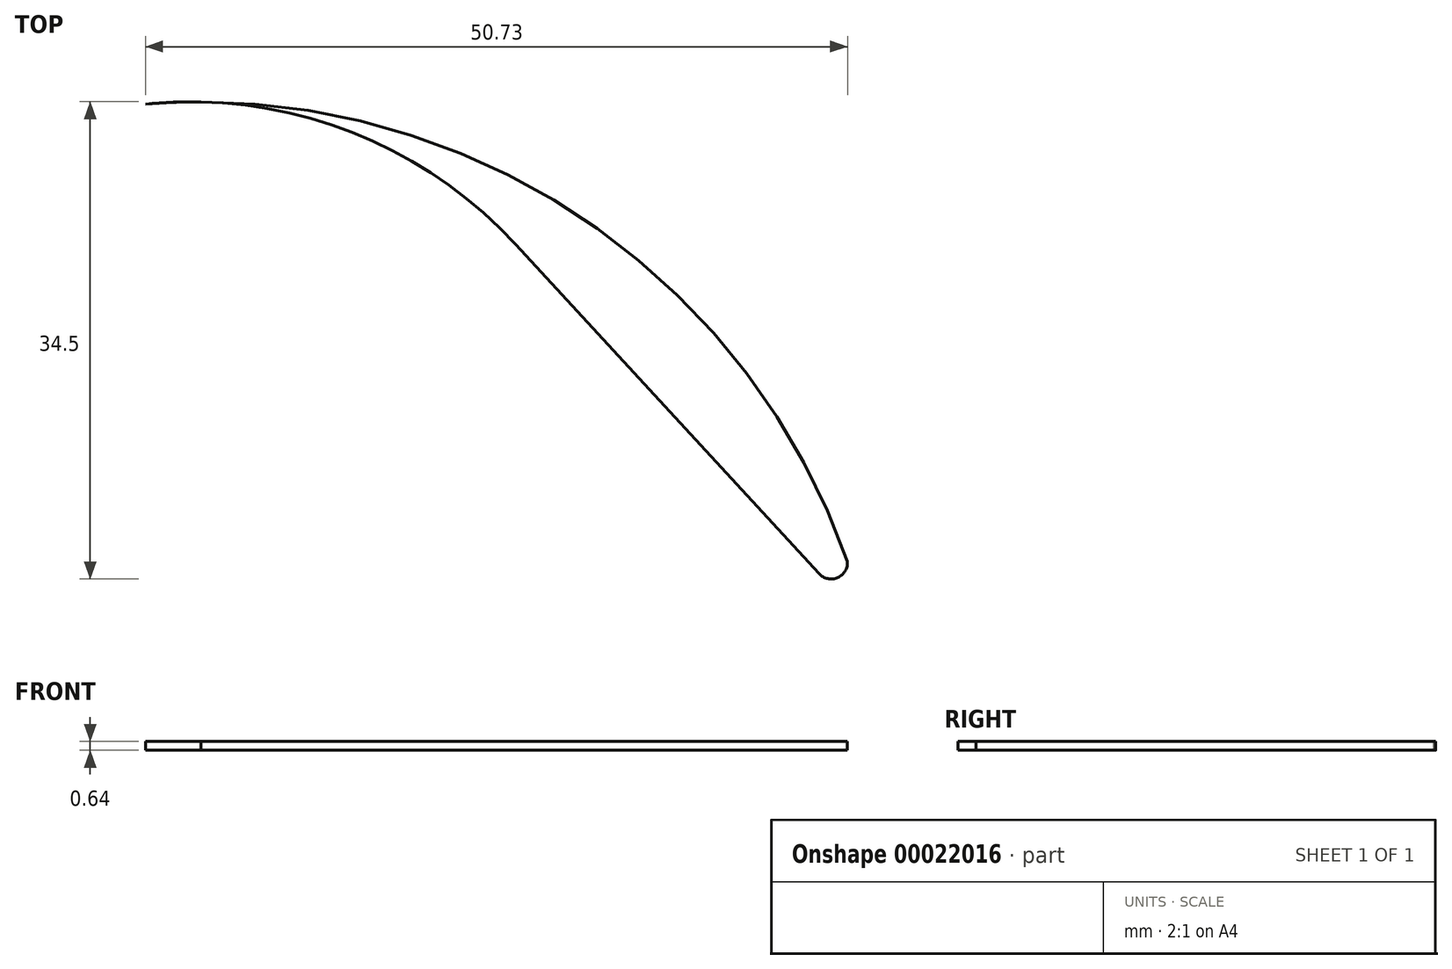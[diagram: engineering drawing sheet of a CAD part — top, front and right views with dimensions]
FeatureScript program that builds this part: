
annotation { "Feature Type Name" : "Feature", "Feature Type Description" : "" }
export const myFeature = defineFeature(function(context is Context, id is Id, definition is map)
    precondition{}
    {
        {
            var Q0;
            Q0=qCreatedBy(makeId("Top.planeOp"),FACE);
            var sketch = newSketch(context, id + "F0", { "sketchPlane" : qUnion([Q0])});
            skLineSegment(sketch, "E0", {"start": v(0, 0) * mm, "end": v(-21.95, 23.82) * mm});
            skArc(sketch, "E1", {"start": v(0, 0) * mm, "mid": v(1.35, -0.28) * mm, "end": v(2.05, 0.9) * mm});
            skLineSegment(sketch, "E2", {"start": v(0, 0) * mm, "end": v(2.05, 0.9) * mm});
            skArc(sketch, "E3", {"start": v(-21.95, 23.82) * mm, "mid": v(-34.11, 32.05) * mm, "end": v(-48.67, 33.95) * mm});
            skArc(sketch, "E4", {"start": v(2.05, 0.9) * mm, "mid": v(-17.68, 26.08) * mm, "end": v(-48.67, 33.95) * mm});
            skSolve(sketch);
        }
        {
            var Q0;
            Q0 = qSketchRegion(id + "F0", true);
            extrude(context, id + "F1", {"entities" : qUnion([Q0]), "depth" : 0.64 * mm});
        }
        {
            var Q0;
            Q0 = qSketchRegion(id + "F0", true);
            extrude(context, id + "F2", {"entities" : qUnion([Q0]), "depth" : 0.64 * mm});
        }
    });
